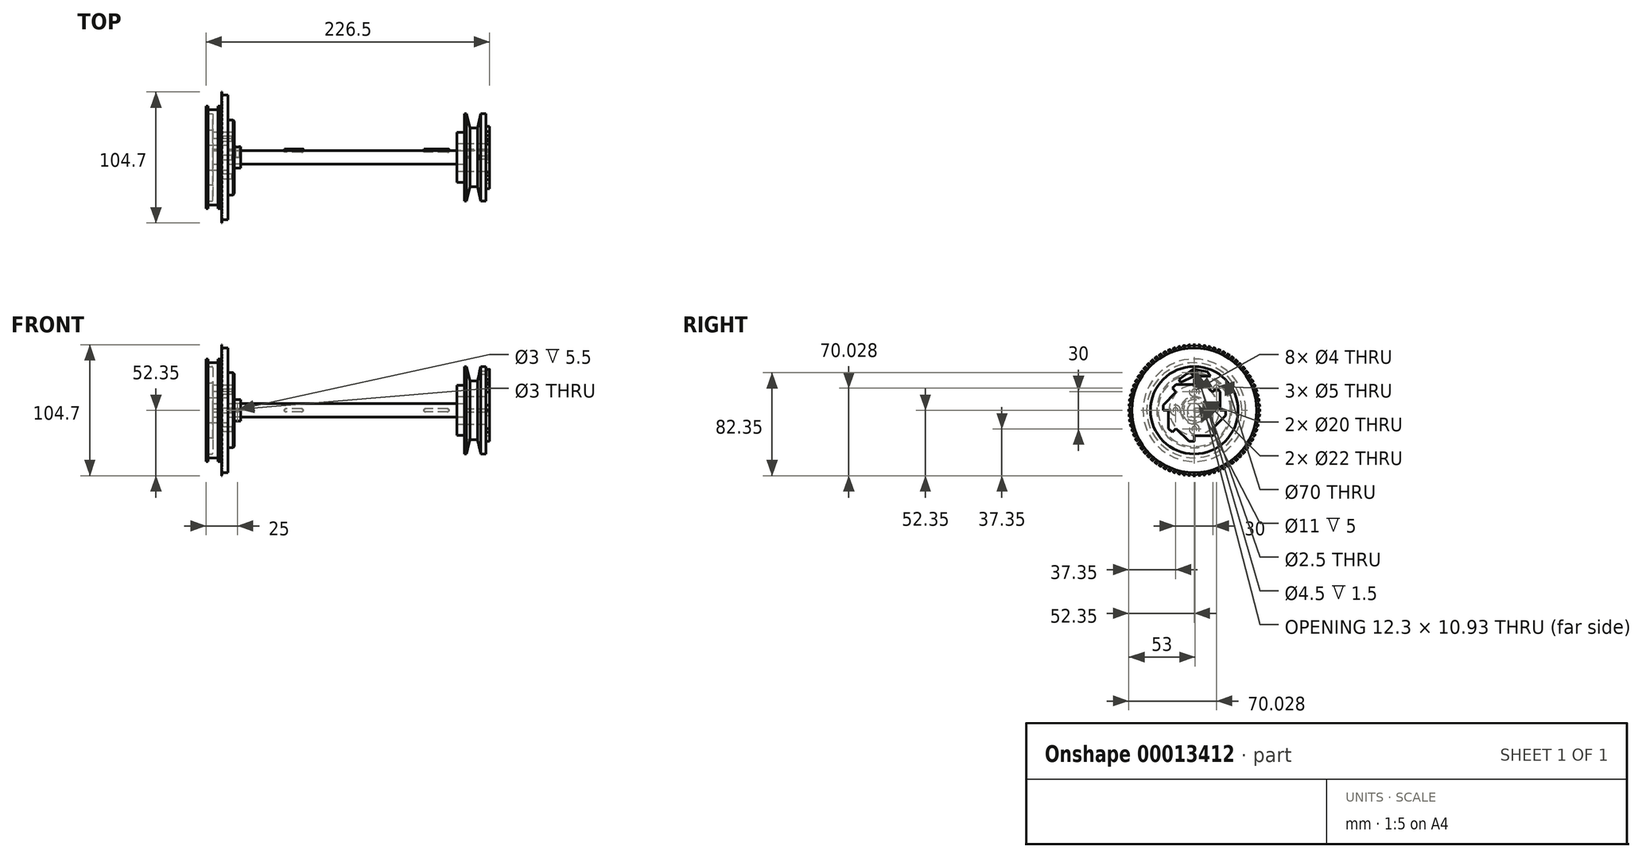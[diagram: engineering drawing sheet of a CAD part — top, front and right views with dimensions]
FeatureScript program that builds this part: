
annotation { "Feature Type Name" : "Feature", "Feature Type Description" : "" }
export const myFeature = defineFeature(function(context is Context, id is Id, definition is map)
    precondition{}
    {
        {
            var Q0;
            Q0=qCreatedBy(makeId("Right.planeOp"),FACE);
            var sketch = newSketch(context, id + "F0", { "sketchPlane" : qUnion([Q0])});
            skCircle(sketch, "E0", {"center": v(0, 0) * mm, "radius": 5.5 * mm});
            skSolve(sketch);
        }
        {
            var Q0;
            Q0=makeQuery(id+"F0.imprint","IMPRINT",FACE,{"disambiguationData":[TD([[makeQuery(id+"F0.imprint","IMPRINT",EDGE,{"derivedFrom":sQuery(id+"F0.wireOp",EDGE,"E0")}),1.0]])]});
            extrude(context, id + "F1", {"entities" : qUnion([Q0]), "endBound" : BoundingType.SYMMETRIC, "depth" : 204 * mm});
        }
        {
            var Q0;
            Q0=qCreatedBy(makeId("Front.planeOp"),FACE);
            cPlane(context, id + "F2", {"entities" : qUnion([Q0]), "cplaneType" : CPlaneType.OFFSET, "offset" : 5.5 * mm, "oppositeDirection" : true, "width" : 150 * mm, "height" : 150 * mm});
        }
        {
            var Q0;
            Q0=qCreatedBy(id+"F2.planeOp",FACE);
            var sketch = newSketch(context, id + "F3", { "sketchPlane" : qUnion([Q0])});
            skLineSegment(sketch, "E1.0", {"start": v(102, 5.5) * mm, "end": v(102, -5.5) * mm});
            skLineSegment(sketch, "E1.1", {"start": v(-102, 5.5) * mm, "end": v(-102, -5.5) * mm});
            skLineSegment(sketch, "E2", {"start": v(102, 0) * mm, "end": v(69.5, 0) * mm, "construction": true});
            skCircle(sketch, "E3", {"center": v(68.25, 0) * mm, "radius": 1.25 * mm});
            skCircle(sketch, "E4", {"center": v(50.75, 0) * mm, "radius": 1.25 * mm});
            skLineSegment(sketch, "E5", {"start": v(68.25, 1.25) * mm, "end": v(50.75, 1.25) * mm});
            skLineSegment(sketch, "E6", {"start": v(68.25, -1.25) * mm, "end": v(50.75, -1.25) * mm});
            skLineSegment(sketch, "E7", {"start": v(-102, 0) * mm, "end": v(-62, 0) * mm, "construction": true});
            skCircle(sketch, "E8", {"center": v(-60.75, 0) * mm, "radius": 1.25 * mm});
            skCircle(sketch, "E9", {"center": v(-48.25, 0) * mm, "radius": 1.25 * mm});
            skLineSegment(sketch, "E10", {"start": v(-48.25, 1.25) * mm, "end": v(-60.75, 1.25) * mm});
            skLineSegment(sketch, "E11", {"start": v(-48.25, -1.25) * mm, "end": v(-60.75, -1.25) * mm});
            skSolve(sketch);
        }
        {
            var Q0;
            {var subQ1=sQuery(id+"F3.wireOp",EDGE,"E5");Q0=makeQuery(id+"F3.imprint","IMPRINT",FACE,{"disambiguationData":[TD([[makeQuery(id+"F3.imprint","IMPRINT",EDGE,{"derivedFrom":subQ1}),1.0]])]});}
            var Q1;
            {var subQ0=sQuery(id+"F3.wireOp",EDGE,"E3");var subQ2=makeQuery(id+"F3.imprint","INTERSECT",VERTEX,{"derivedFrom":[subQ0,sQuery(id+"F3.wireOp",EDGE,"E5")]});Q1=makeQuery(id+"F3.imprint","IMPRINT",FACE,{"disambiguationData":[TD([[makeQuery(id+"F3.imprint","IMPRINT",EDGE,{"disambiguationData":[TD([[subQ2,-1.0]])],"derivedFrom":subQ0}),1.0]])]});}
            var Q2;
            {var subQ0=sQuery(id+"F3.wireOp",EDGE,"E4");var subQ2=makeQuery(id+"F3.imprint","INTERSECT",VERTEX,{"derivedFrom":[subQ0,sQuery(id+"F3.wireOp",EDGE,"E5")]});Q2=makeQuery(id+"F3.imprint","IMPRINT",FACE,{"disambiguationData":[TD([[makeQuery(id+"F3.imprint","IMPRINT",EDGE,{"disambiguationData":[TD([[subQ2,-1.0]])],"derivedFrom":subQ0}),1.0]])]});}
            var Q3;
            {var subQ0=sQuery(id+"F3.wireOp",EDGE,"E9");var subQ2=makeQuery(id+"F3.imprint","INTERSECT",VERTEX,{"derivedFrom":[subQ0,sQuery(id+"F3.wireOp",EDGE,"E10")]});Q3=makeQuery(id+"F3.imprint","IMPRINT",FACE,{"disambiguationData":[TD([[makeQuery(id+"F3.imprint","IMPRINT",EDGE,{"disambiguationData":[TD([[subQ2,-1.0]])],"derivedFrom":subQ0}),1.0]])]});}
            var Q4;
            {var subQ1=sQuery(id+"F3.wireOp",EDGE,"E10");Q4=makeQuery(id+"F3.imprint","IMPRINT",FACE,{"disambiguationData":[TD([[makeQuery(id+"F3.imprint","IMPRINT",EDGE,{"derivedFrom":subQ1}),1.0]])]});}
            var Q5;
            {var subQ0=sQuery(id+"F3.wireOp",EDGE,"E8");var subQ2=makeQuery(id+"F3.imprint","INTERSECT",VERTEX,{"derivedFrom":[subQ0,sQuery(id+"F3.wireOp",EDGE,"E10")]});Q5=makeQuery(id+"F3.imprint","IMPRINT",FACE,{"disambiguationData":[TD([[makeQuery(id+"F3.imprint","IMPRINT",EDGE,{"disambiguationData":[TD([[subQ2,-1.0]])],"derivedFrom":subQ0}),1.0]])]});}
            extrude(context, id + "F4", {"entities" : qUnion([Q0, Q1, Q2, Q3, Q4, Q5]), "operationType" : NewBodyOperationType.REMOVE, "depth" : 1.3 * mm});
        }
        {
            var Q0;
            {var subQ0=sQuery(id+"F3.wireOp",EDGE,"E3");var subQ2=makeQuery(id+"F3.imprint","INTERSECT",VERTEX,{"derivedFrom":[subQ0,sQuery(id+"F3.wireOp",EDGE,"E5")]});Q0=makeQuery(id+"F3.imprint","IMPRINT",FACE,{"disambiguationData":[TD([[makeQuery(id+"F3.imprint","IMPRINT",EDGE,{"disambiguationData":[TD([[subQ2,-1.0]])],"derivedFrom":subQ0}),1.0]])]});}
            var Q1;
            {var subQ1=sQuery(id+"F3.wireOp",EDGE,"E5");Q1=makeQuery(id+"F3.imprint","IMPRINT",FACE,{"disambiguationData":[TD([[makeQuery(id+"F3.imprint","IMPRINT",EDGE,{"derivedFrom":subQ1}),1.0]])]});}
            var Q2;
            {var subQ0=sQuery(id+"F3.wireOp",EDGE,"E4");var subQ2=makeQuery(id+"F3.imprint","INTERSECT",VERTEX,{"derivedFrom":[subQ0,sQuery(id+"F3.wireOp",EDGE,"E5")]});Q2=makeQuery(id+"F3.imprint","IMPRINT",FACE,{"disambiguationData":[TD([[makeQuery(id+"F3.imprint","IMPRINT",EDGE,{"disambiguationData":[TD([[subQ2,-1.0]])],"derivedFrom":subQ0}),1.0]])]});}
            var Q3;
            {var subQ0=sQuery(id+"F3.wireOp",EDGE,"E9");var subQ2=makeQuery(id+"F3.imprint","INTERSECT",VERTEX,{"derivedFrom":[subQ0,sQuery(id+"F3.wireOp",EDGE,"E10")]});Q3=makeQuery(id+"F3.imprint","IMPRINT",FACE,{"disambiguationData":[TD([[makeQuery(id+"F3.imprint","IMPRINT",EDGE,{"disambiguationData":[TD([[subQ2,-1.0]])],"derivedFrom":subQ0}),1.0]])]});}
            var Q4;
            {var subQ1=sQuery(id+"F3.wireOp",EDGE,"E10");Q4=makeQuery(id+"F3.imprint","IMPRINT",FACE,{"disambiguationData":[TD([[makeQuery(id+"F3.imprint","IMPRINT",EDGE,{"derivedFrom":subQ1}),1.0]])]});}
            var Q5;
            {var subQ0=sQuery(id+"F3.wireOp",EDGE,"E8");var subQ2=makeQuery(id+"F3.imprint","INTERSECT",VERTEX,{"derivedFrom":[subQ0,sQuery(id+"F3.wireOp",EDGE,"E10")]});Q5=makeQuery(id+"F3.imprint","IMPRINT",FACE,{"disambiguationData":[TD([[makeQuery(id+"F3.imprint","IMPRINT",EDGE,{"disambiguationData":[TD([[subQ2,-1.0]])],"derivedFrom":subQ0}),1.0]])]});}
            extrude(context, id + "F5", {"entities" : qUnion([Q0, Q1, Q2, Q3, Q4, Q5]), "endBound" : BoundingType.SYMMETRIC, "depth" : 2.5 * mm});
        }
        {
            var Q0;
            Q0=makeQuery(id+"F1.opExtrude","CAP_FACE",FACE,{"disambiguationData":[OSD([sQuery(id+"F0.wireOp",EDGE,"E0")])],"isStart":true});
            var sketch = newSketch(context, id + "F6", { "sketchPlane" : qUnion([Q0])});
            skCircle(sketch, "E12", {"center": v(0, 0) * mm, "radius": 10 * mm});
            skCircle(sketch, "E13", {"center": v(0, 0) * mm, "radius": 30 * mm});
            skLineSegment(sketch, "E14", {"start": v(0, 0) * mm, "end": v(0, -15) * mm, "construction": true});
            skLineSegment(sketch, "E15", {"start": v(0, 0) * mm, "end": v(-17.68, 17.68) * mm, "construction": true});
            skLineSegment(sketch, "E16", {"start": v(0, 0) * mm, "end": v(-5.5, 0) * mm, "construction": true});
            skCircle(sketch, "E17", {"center": v(0, -15) * mm, "radius": 2 * mm});
            skCircle(sketch, "E18", {"center": v(-17.68, 17.68) * mm, "radius": 2.5 * mm});
            skLineSegment(sketch, "E19.rect.bottom", {"start": v(-6.8, -1.25) * mm, "end": v(-4.2, -1.25) * mm});
            skLineSegment(sketch, "E19.rect.top", {"start": v(-6.8, 1.25) * mm, "end": v(-4.2, 1.25) * mm});
            skLineSegment(sketch, "E19.rect.left", {"start": v(-6.8, -1.25) * mm, "end": v(-6.8, 1.25) * mm});
            skLineSegment(sketch, "E19.rect.right", {"start": v(-4.2, -1.25) * mm, "end": v(-4.2, 1.25) * mm});
            skPoint(sketch, "E19.rect.middle", {"position": v(-5.5, 0) * mm});
            skCircle(sketch, "E20.1.0", {"center": v(15, 0) * mm, "radius": 2 * mm});
            skCircle(sketch, "E20.2.0", {"center": v(0, 15) * mm, "radius": 2 * mm});
            skCircle(sketch, "E20.3.0", {"center": v(-15, 0) * mm, "radius": 2 * mm});
            skSolve(sketch);
        }
        {
            var Q0;
            Q0=makeQuery(id+"F6.imprint","IMPRINT",FACE,{"disambiguationData":[TD([[makeQuery(id+"F6.imprint","IMPRINT",EDGE,{"derivedFrom":sQuery(id+"F6.wireOp",EDGE,"E12")}),-1.0]])]});
            extrude(context, id + "F7", {"entities" : qUnion([Q0]), "depth" : 5 * mm});
        }
        {
            var Q0;
            Q0=makeQuery(id+"F6.imprint","IMPRINT",FACE,{"disambiguationData":[TD([[makeQuery(id+"F6.imprint","IMPRINT",EDGE,{"derivedFrom":sQuery(id+"F6.wireOp",EDGE,"E12")}),1.0]])]});
            extrude(context, id + "F8", {"entities" : qUnion([Q0]), "operationType" : NewBodyOperationType.ADD, "depth" : 17 * mm});
        }
        {
            var Q0;
            Q0=makeQuery(id+"F7.opExtrude","CAP_EDGE",EDGE,{"disambiguationData":[OSD([sQuery(id+"F6.wireOp",EDGE,"E13")])],"isStart":true});
            chamfer(context, id + "F9", {"entities" : qUnion([Q0]), "width" : 1 * mm, "tangentPropagation" : true});
        }
        {
            var Q0;
            Q0=makeQuery(id+"F7.opExtrude","CAP_EDGE",EDGE,{"disambiguationData":[OSD([sQuery(id+"F6.wireOp",EDGE,"E20.1.0")])],"isStart":true});
            var Q1;
            Q1=makeQuery(id+"F7.opExtrude","CAP_EDGE",EDGE,{"disambiguationData":[OSD([sQuery(id+"F6.wireOp",EDGE,"E17")])],"isStart":true});
            var Q2;
            Q2=makeQuery(id+"F7.opExtrude","CAP_EDGE",EDGE,{"disambiguationData":[OSD([sQuery(id+"F6.wireOp",EDGE,"E20.3.0")])],"isStart":true});
            var Q3;
            Q3=makeQuery(id+"F7.opExtrude","CAP_EDGE",EDGE,{"disambiguationData":[OSD([sQuery(id+"F6.wireOp",EDGE,"E20.2.0")])],"isStart":true});
            chamfer(context, id + "F10", {"entities" : qUnion([Q0, Q1, Q2, Q3]), "width" : 2 * mm, "tangentPropagation" : true});
        }
        {
            var Q0;
            Q0=makeQuery(id+"F1.opExtrude","CAP_FACE",FACE,{"disambiguationData":[OSD([sQuery(id+"F0.wireOp",EDGE,"E0")])],"isStart":false});
            var sketch = newSketch(context, id + "F11", { "sketchPlane" : qUnion([Q0])});
            skLineSegment(sketch, "E21.0", {"start": v(4.25, 1.25) * mm, "end": v(6.75, 1.25) * mm});
            skLineSegment(sketch, "E21.1", {"start": v(4.25, -1.25) * mm, "end": v(6.75, -1.25) * mm});
            skCircle(sketch, "E22", {"center": v(0, 0) * mm, "radius": 11 * mm});
            skCircle(sketch, "E23", {"center": v(0, 0) * mm, "radius": 20.5 * mm});
            skCircle(sketch, "E24", {"center": v(0, 0) * mm, "radius": 25.25 * mm});
            skLineSegment(sketch, "E25", {"start": v(0, 0) * mm, "end": v(5.5, 0) * mm, "construction": true});
            skLineSegment(sketch, "E26.rect.bottom", {"start": v(6.8, -1.25) * mm, "end": v(4.2, -1.25) * mm});
            skLineSegment(sketch, "E26.rect.top", {"start": v(6.8, 1.25) * mm, "end": v(4.2, 1.25) * mm});
            skLineSegment(sketch, "E26.rect.left", {"start": v(6.8, -1.25) * mm, "end": v(6.8, 1.25) * mm});
            skLineSegment(sketch, "E26.rect.right", {"start": v(4.2, -1.25) * mm, "end": v(4.2, 1.25) * mm});
            skPoint(sketch, "E26.rect.middle", {"position": v(5.5, 0) * mm});
            skLineSegment(sketch, "E27", {"start": v(20.5, 0) * mm, "end": v(25.25, 0) * mm});
            skLineSegment(sketch, "E28.1.0", {"start": v(14.5, 14.5) * mm, "end": v(17.85, 17.85) * mm});
            skLineSegment(sketch, "E28.2.0", {"start": v(0, 20.5) * mm, "end": v(0, 25.25) * mm});
            skLineSegment(sketch, "E28.3.0", {"start": v(-14.5, 14.5) * mm, "end": v(-17.85, 17.85) * mm});
            skLineSegment(sketch, "E28.4.0", {"start": v(-20.5, 0) * mm, "end": v(-25.25, 0) * mm});
            skLineSegment(sketch, "E28.5.0", {"start": v(-14.5, -14.5) * mm, "end": v(-17.85, -17.85) * mm});
            skLineSegment(sketch, "E28.6.0", {"start": v(0, -20.5) * mm, "end": v(0, -25.25) * mm});
            skLineSegment(sketch, "E28.7.0", {"start": v(14.5, -14.5) * mm, "end": v(17.85, -17.85) * mm});
            skLineSegment(sketch, "E29", {"start": v(0, -20.5) * mm, "end": v(14.74, -20.5) * mm});
            skLineSegment(sketch, "E30", {"start": v(14.74, -20.5) * mm, "end": v(17.62, -17.62) * mm});
            skLineSegment(sketch, "E31.1.0", {"start": v(14.5, -14.5) * mm, "end": v(24.92, -4.07) * mm});
            skLineSegment(sketch, "E31.1.1", {"start": v(24.92, -4.07) * mm, "end": v(24.92, 0) * mm});
            skLineSegment(sketch, "E31.2.0", {"start": v(20.5, 0) * mm, "end": v(20.5, 14.74) * mm});
            skLineSegment(sketch, "E31.2.1", {"start": v(20.5, 14.74) * mm, "end": v(17.62, 17.62) * mm});
            skLineSegment(sketch, "E31.3.0", {"start": v(14.5, 14.5) * mm, "end": v(4.07, 24.92) * mm});
            skLineSegment(sketch, "E31.3.1", {"start": v(4.07, 24.92) * mm, "end": v(0, 24.92) * mm});
            skLineSegment(sketch, "E31.4.0", {"start": v(0, 20.5) * mm, "end": v(-14.74, 20.5) * mm});
            skLineSegment(sketch, "E31.4.1", {"start": v(-14.74, 20.5) * mm, "end": v(-17.62, 17.62) * mm});
            skLineSegment(sketch, "E31.5.0", {"start": v(-14.5, 14.5) * mm, "end": v(-24.92, 4.07) * mm});
            skLineSegment(sketch, "E31.5.1", {"start": v(-24.92, 4.07) * mm, "end": v(-24.92, 0) * mm});
            skLineSegment(sketch, "E31.6.0", {"start": v(-20.5, 0) * mm, "end": v(-20.5, -14.74) * mm});
            skLineSegment(sketch, "E31.6.1", {"start": v(-20.5, -14.74) * mm, "end": v(-17.62, -17.62) * mm});
            skLineSegment(sketch, "E31.7.0", {"start": v(-14.5, -14.5) * mm, "end": v(-4.07, -24.92) * mm});
            skLineSegment(sketch, "E31.7.1", {"start": v(-4.07, -24.92) * mm, "end": v(0, -24.92) * mm});
            skSolve(sketch);
        }
        {
            var Q0;
            {var subQ1=sQuery(id+"F11.wireOp",EDGE,"E31.5.0");Q0=makeQuery(id+"F11.imprint","IMPRINT",FACE,{"disambiguationData":[TD([[makeQuery(id+"F11.imprint","IMPRINT",EDGE,{"derivedFrom":subQ1}),1.0]])]});}
            var Q1;
            {var subQ1=sQuery(id+"F11.wireOp",EDGE,"E31.4.0");Q1=makeQuery(id+"F11.imprint","IMPRINT",FACE,{"disambiguationData":[TD([[makeQuery(id+"F11.imprint","IMPRINT",EDGE,{"derivedFrom":subQ1}),1.0]])]});}
            var Q2;
            {var subQ1=sQuery(id+"F11.wireOp",EDGE,"E31.3.0");Q2=makeQuery(id+"F11.imprint","IMPRINT",FACE,{"disambiguationData":[TD([[makeQuery(id+"F11.imprint","IMPRINT",EDGE,{"derivedFrom":subQ1}),1.0]])]});}
            var Q3;
            {var subQ1=sQuery(id+"F11.wireOp",EDGE,"E31.2.0");Q3=makeQuery(id+"F11.imprint","IMPRINT",FACE,{"disambiguationData":[TD([[makeQuery(id+"F11.imprint","IMPRINT",EDGE,{"derivedFrom":subQ1}),1.0]])]});}
            var Q4;
            {var subQ1=sQuery(id+"F11.wireOp",EDGE,"E31.1.0");Q4=makeQuery(id+"F11.imprint","IMPRINT",FACE,{"disambiguationData":[TD([[makeQuery(id+"F11.imprint","IMPRINT",EDGE,{"derivedFrom":subQ1}),1.0]])]});}
            var Q5;
            {var subQ1=sQuery(id+"F11.wireOp",EDGE,"E29");Q5=makeQuery(id+"F11.imprint","IMPRINT",FACE,{"disambiguationData":[TD([[makeQuery(id+"F11.imprint","IMPRINT",EDGE,{"derivedFrom":subQ1}),1.0]])]});}
            var Q6;
            {var subQ1=sQuery(id+"F11.wireOp",EDGE,"E31.7.0");Q6=makeQuery(id+"F11.imprint","IMPRINT",FACE,{"disambiguationData":[TD([[makeQuery(id+"F11.imprint","IMPRINT",EDGE,{"derivedFrom":subQ1}),1.0]])]});}
            var Q7;
            {var subQ1=sQuery(id+"F11.wireOp",EDGE,"E31.6.0");Q7=makeQuery(id+"F11.imprint","IMPRINT",FACE,{"disambiguationData":[TD([[makeQuery(id+"F11.imprint","IMPRINT",EDGE,{"derivedFrom":subQ1}),1.0]])]});}
            var Q8;
            Q8=makeQuery(id+"F11.imprint","IMPRINT",FACE,{"disambiguationData":[TD([[makeQuery(id+"F11.imprint","IMPRINT",EDGE,{"derivedFrom":sQuery(id+"F11.wireOp",EDGE,"E22")}),-1.0]])]});
            extrude(context, id + "F12", {"entities" : qUnion([Q0, Q1, Q2, Q3, Q4, Q5, Q6, Q7, Q8]), "oppositeDirection" : true, "depth" : 3 * mm});
        }
        {
            var Q0;
            Q0=makeQuery(id+"F11.imprint","IMPRINT",FACE,{"disambiguationData":[TD([[makeQuery(id+"F11.imprint","IMPRINT",EDGE,{"derivedFrom":sQuery(id+"F11.wireOp",EDGE,"E22")}),1.0]])]});
            extrude(context, id + "F13", {"entities" : qUnion([Q0]), "operationType" : NewBodyOperationType.ADD, "oppositeDirection" : true, "depth" : 20 * mm});
        }
        {
            var Q0;
            Q0=makeQuery(id+"F7.opExtrude","CAP_FACE",FACE,{"disambiguationData":[OSD([sQuery(id+"F6.wireOp",EDGE,"E12"),sQuery(id+"F6.wireOp",EDGE,"E13"),sQuery(id+"F6.wireOp",EDGE,"E17"),sQuery(id+"F6.wireOp",EDGE,"E18"),sQuery(id+"F6.wireOp",EDGE,"E20.1.0"),sQuery(id+"F6.wireOp",EDGE,"E20.2.0"),sQuery(id+"F6.wireOp",EDGE,"E20.3.0")])],"isStart":false});
            var sketch = newSketch(context, id + "F14", { "sketchPlane" : qUnion([Q0])});
            skCircle(sketch, "E32", {"center": v(0, 0) * mm, "radius": 52.35 * mm});
            skCircle(sketch, "E33", {"center": v(0, 0) * mm, "radius": 51.1 * mm, "construction": true});
            skCircle(sketch, "E34", {"center": v(0, 0) * mm, "radius": 49.85 * mm});
            skLineSegment(sketch, "E35", {"start": v(0, 0) * mm, "end": v(0, 52.35) * mm, "construction": true});
            skLineSegment(sketch, "E36", {"start": v(0, 49.85) * mm, "end": v(15, 49.85) * mm, "construction": true});
            skLineSegment(sketch, "E37", {"start": v(0, 0) * mm, "end": v(-1, 51.1) * mm, "construction": true});
            skLineSegment(sketch, "E38", {"start": v(0, 0) * mm, "end": v(-3.15, 49.75) * mm, "construction": true});
            skArc(sketch, "E39", {"start": v(-0.86, 52.34) * mm, "mid": v(-1, 51.1) * mm, "end": v(-1.05, 49.84) * mm});
            skArc(sketch, "E40.0.MirrorCS", {"start": v(0.86, 52.34) * mm, "mid": v(1, 51.1) * mm, "end": v(1.05, 49.84) * mm});
            skSolve(sketch);
        }
        {
            var Q0;
            Q0=makeQuery(id+"F14.imprint","IMPRINT",FACE,{"disambiguationData":[TD([[makeQuery(id+"F14.imprint","IMPRINT",EDGE,{"derivedFrom":makeQuery(id+"F7.opExtrude","CAP_EDGE",EDGE,{"disambiguationData":[OSD([sQuery(id+"F6.wireOp",EDGE,"E13")])],"isStart":false})}),-1.0]])]});
            var Q1;
            {var subQ1=sQuery(id+"F14.wireOp",EDGE,"E39");Q1=makeQuery(id+"F14.imprint","IMPRINT",FACE,{"disambiguationData":[TD([[makeQuery(id+"F14.imprint","IMPRINT",EDGE,{"derivedFrom":subQ1}),1.0]])]});}
            var Q2;
            Q2=makeQuery(id+"F14.imprint","IMPRINT",FACE,{"disambiguationData":[TD([[makeQuery(id+"F14.imprint","IMPRINT",EDGE,{"derivedFrom":makeQuery(id+"F7.opExtrude","CAP_EDGE",EDGE,{"disambiguationData":[OSD([sQuery(id+"F6.wireOp",EDGE,"E13")])],"isStart":false})}),1.0]])]});
            extrude(context, id + "F15", {"entities" : qUnion([Q0, Q1, Q2]), "depth" : 5 * mm});
        }
        {
            var Q0;
            Q0=makeQuery(id+"F15.opExtrude","SWEPT_FACE",FACE,{"disambiguationData":[OSD([sQuery(id+"F14.wireOp",EDGE,"E40.0.MirrorCS")])]});
            var Q1;
            Q1=makeQuery(id+"F15.opExtrude","SWEPT_FACE",FACE,{"disambiguationData":[OSD([sQuery(id+"F14.wireOp",EDGE,"E32")])]});
            var Q2;
            Q2=makeQuery(id+"F15.opExtrude","SWEPT_FACE",FACE,{"disambiguationData":[OSD([sQuery(id+"F14.wireOp",EDGE,"E39")])]});
            var Q3;
            Q3=makeQuery(id+"F8.opExtrude","CAP_EDGE",EDGE,{"disambiguationData":[OSD([sQuery(id+"F6.wireOp",EDGE,"E12")])],"isStart":false});
            circularPattern(context, id + "F16", {"faces" : qUnion([Q0, Q1, Q2]), "axis" : qUnion([Q3]), "angle" : 4.5 * degree, "instanceCount" : round(80), "patternType" : PatternType.FACE});
        }
        {
            var Q0;
            Q0=qCreatedBy(makeId("Front.planeOp"),FACE);
            var sketch = newSketch(context, id + "F17", { "sketchPlane" : qUnion([Q0])});
            skLineSegment(sketch, "E41.0", {"start": v(-107, -30) * mm, "end": v(-107, 30) * mm});
            skLineSegment(sketch, "E42", {"start": v(-107, 0) * mm, "end": v(-134.37, 0) * mm, "construction": true});
            skLineSegment(sketch, "E43", {"start": v(-107, 0) * mm, "end": v(-107, 49.85) * mm, "construction": true});
            skLineSegment(sketch, "E44.bottom", {"start": v(-107, 49.85) * mm, "end": v(-112, 49.85) * mm});
            skLineSegment(sketch, "E44.top", {"start": v(-107, 52.35) * mm, "end": v(-112, 52.35) * mm});
            skLineSegment(sketch, "E44.left", {"start": v(-107, 49.85) * mm, "end": v(-107, 52.35) * mm});
            skLineSegment(sketch, "E44.right", {"start": v(-112, 49.85) * mm, "end": v(-112, 52.35) * mm});
            skLineSegment(sketch, "E45", {"start": v(-109.5, 52.35) * mm, "end": v(-109.5, 49.85) * mm, "construction": true});
            skLineSegment(sketch, "E46", {"start": v(-107, 49.85) * mm, "end": v(-117, 49.85) * mm, "construction": true});
            skLineSegment(sketch, "E47", {"start": v(-107, 51.1) * mm, "end": v(-112, 51.1) * mm, "construction": true});
            skArc(sketch, "E48", {"start": v(-107, 51.1) * mm, "mid": v(-107.1, 51.73) * mm, "end": v(-107.24, 52.35) * mm});
            skArc(sketch, "E49.0.MirrorCS", {"start": v(-112, 51.1) * mm, "mid": v(-111.9, 51.73) * mm, "end": v(-111.76, 52.35) * mm});
            skSolve(sketch);
        }
        {
            var Q0;
            {var subQ0=sQuery(id+"F17.wireOp",EDGE,"E49.0.MirrorCS");Q0=makeQuery(id+"F17.imprint","IMPRINT",FACE,{"disambiguationData":[TD([[makeQuery(id+"F17.imprint","IMPRINT",EDGE,{"derivedFrom":subQ0}),1.0]])]});}
            var Q1;
            {var subQ0=sQuery(id+"F17.wireOp",EDGE,"E48");Q1=makeQuery(id+"F17.imprint","IMPRINT",FACE,{"disambiguationData":[TD([[makeQuery(id+"F17.imprint","IMPRINT",EDGE,{"derivedFrom":subQ0}),-1.0]])]});}
            var Q2;
            Q2=sQuery(id+"F17.wireOp",EDGE,"E42");
            revolve(context, id + "F18", {"operationType" : NewBodyOperationType.REMOVE, "entities" : qUnion([Q0, Q1]), "axis" : qUnion([Q2]), "revolveType" : RevolveType.FULL, "oppositeDirection" : true});
        }
        {
            var Q0;
            Q0=qCreatedBy(makeId("Front.planeOp"),FACE);
            var sketch = newSketch(context, id + "F19", { "sketchPlane" : qUnion([Q0])});
            skLineSegment(sketch, "E50.0", {"start": v(-112, -10) * mm, "end": v(-112, 10) * mm});
            skLineSegment(sketch, "E51", {"start": v(-112, 0) * mm, "end": v(-131.3, 0) * mm, "construction": true});
            skLineSegment(sketch, "E52", {"start": v(-112, 10) * mm, "end": v(-112, 22) * mm});
            skLineSegment(sketch, "E53", {"start": v(-112, 22) * mm, "end": v(-113.5, 22) * mm});
            skLineSegment(sketch, "E54", {"start": v(-113.5, 22) * mm, "end": v(-113.5, 41) * mm});
            skLineSegment(sketch, "E55", {"start": v(-113.5, 41) * mm, "end": v(-115, 41) * mm});
            skLineSegment(sketch, "E56", {"start": v(-115, 41) * mm, "end": v(-115, 38) * mm});
            skLineSegment(sketch, "E57", {"start": v(-115, 38) * mm, "end": v(-123, 38) * mm});
            skLineSegment(sketch, "E58", {"start": v(-123, 38) * mm, "end": v(-123, 41) * mm});
            skLineSegment(sketch, "E59", {"start": v(-123, 41) * mm, "end": v(-124.5, 41) * mm});
            skLineSegment(sketch, "E60", {"start": v(-124.5, 41) * mm, "end": v(-124.5, 35) * mm});
            skLineSegment(sketch, "E61", {"start": v(-124.5, 35) * mm, "end": v(-119, 35) * mm});
            skLineSegment(sketch, "E62", {"start": v(-119, 35) * mm, "end": v(-119, 22) * mm});
            skLineSegment(sketch, "E63", {"start": v(-119, 22) * mm, "end": v(-124.5, 22) * mm});
            skLineSegment(sketch, "E64", {"start": v(-124.5, 22) * mm, "end": v(-124.5, 10) * mm});
            skLineSegment(sketch, "E65", {"start": v(-124.5, 10) * mm, "end": v(-112, 10) * mm});
            skSolve(sketch);
        }
        {
            var Q0;
            Q0=makeQuery(id+"F19.imprint","IMPRINT",FACE,{"disambiguationData":[TD([[makeQuery(id+"F19.imprint","IMPRINT",EDGE,{"derivedFrom":sQuery(id+"F19.wireOp",EDGE,"E52")}),1.0]])]});
            var Q1;
            Q1=sQuery(id+"F19.wireOp",EDGE,"E51");
            revolve(context, id + "F20", {"entities" : qUnion([Q0]), "axis" : qUnion([Q1]), "revolveType" : RevolveType.FULL});
        }
        {
            var Q0;
            Q0=makeQuery(id+"F20.opRevolve","SWEPT_EDGE",EDGE,{"disambiguationData":[OSD([sQuery(id+"F19.wireOp",EDGE,"E53"),sQuery(id+"F19.wireOp",EDGE,"E54")])]});
            var Q1;
            Q1=makeQuery(id+"F20.opRevolve","SWEPT_EDGE",EDGE,{"disambiguationData":[OSD([sQuery(id+"F19.wireOp",EDGE,"E62"),sQuery(id+"F19.wireOp",EDGE,"E63")])]});
            var Q2;
            Q2=makeQuery(id+"F20.opRevolve","SWEPT_EDGE",EDGE,{"disambiguationData":[OSD([sQuery(id+"F19.wireOp",EDGE,"E61"),sQuery(id+"F19.wireOp",EDGE,"E62")])]});
            var Q3;
            Q3=makeQuery(id+"F20.opRevolve","SWEPT_EDGE",EDGE,{"disambiguationData":[OSD([sQuery(id+"F19.wireOp",EDGE,"E63"),sQuery(id+"F19.wireOp",EDGE,"E64")])]});
            var Q4;
            Q4=makeQuery(id+"F20.opRevolve","SWEPT_EDGE",EDGE,{"disambiguationData":[OSD([sQuery(id+"F19.wireOp",EDGE,"E60"),sQuery(id+"F19.wireOp",EDGE,"E61")])]});
            fillet(context, id + "F21", {"entities" : qUnion([Q0, Q1, Q2, Q3, Q4]), "radius" : 1 * mm, "tangentPropagation" : true, "allowEdgeOverflow" : false});
        }
        {
            var Q0;
            Q0=makeQuery(id+"F20.opRevolve","SWEPT_FACE",FACE,{"disambiguationData":[OSD([sQuery(id+"F19.wireOp",EDGE,"E54")])]});
            var sketch = newSketch(context, id + "F22", { "sketchPlane" : qUnion([Q0])});
            skCircle(sketch, "E66.0", {"center": v(17.68, 17.68) * mm, "radius": 2.5 * mm});
            skSolve(sketch);
        }
        {
            var Q0;
            {var subQ0=sQuery(id+"F19.wireOp",EDGE,"E54");var subQ1=makeQuery(id+"F21.opFillet","BLEND_EDGE",EDGE,{"blendedFrom":[makeQuery(id+"F20.opRevolve","SWEPT_EDGE",EDGE,{"disambiguationData":[OSD([sQuery(id+"F19.wireOp",EDGE,"E53"),subQ0])]}),makeQuery(id+"F20.opRevolve","SWEPT_FACE",FACE,{"disambiguationData":[OSD([subQ0])]})],"blendedInto":[makeQuery(id+"F20.opRevolve","SWEPT_FACE",FACE,{"disambiguationData":[OSD([subQ0])]})]});var subQ2=sQuery(id+"F22.wireOp",EDGE,"E66.0");var subQ4=makeQuery(id+"F22.imprint","INTERSECT",VERTEX,{"disambiguationData":[OD(0.0)],"derivedFrom":[subQ1,subQ2]});Q0=makeQuery(id+"F22.imprint","IMPRINT",FACE,{"disambiguationData":[TD([[makeQuery(id+"F22.imprint","IMPRINT",EDGE,{"disambiguationData":[TD([[subQ4,1.0]])],"derivedFrom":subQ2}),1.0]])]});}
            var Q1;
            {var subQ0=sQuery(id+"F19.wireOp",EDGE,"E54");var subQ1=makeQuery(id+"F21.opFillet","BLEND_EDGE",EDGE,{"blendedFrom":[makeQuery(id+"F20.opRevolve","SWEPT_EDGE",EDGE,{"disambiguationData":[OSD([sQuery(id+"F19.wireOp",EDGE,"E53"),subQ0])]}),makeQuery(id+"F20.opRevolve","SWEPT_FACE",FACE,{"disambiguationData":[OSD([subQ0])]})],"blendedInto":[makeQuery(id+"F20.opRevolve","SWEPT_FACE",FACE,{"disambiguationData":[OSD([subQ0])]})]});var subQ2=sQuery(id+"F22.wireOp",EDGE,"E66.0");var subQ4=makeQuery(id+"F22.imprint","INTERSECT",VERTEX,{"disambiguationData":[OD(0.0)],"derivedFrom":[subQ1,subQ2]});Q1=makeQuery(id+"F22.imprint","IMPRINT",FACE,{"disambiguationData":[TD([[makeQuery(id+"F22.imprint","IMPRINT",EDGE,{"disambiguationData":[TD([[subQ4,-1.0]])],"derivedFrom":subQ2}),1.0]])]});}
            extrude(context, id + "F23", {"entities" : qUnion([Q0, Q1]), "operationType" : NewBodyOperationType.REMOVE, "endBound" : BoundingType.SYMMETRIC, "oppositeDirection" : true, "depth" : 13 * mm});
        }
        {
            var Q0;
            Q0=qCreatedBy(makeId("Front.planeOp"),FACE);
            var sketch = newSketch(context, id + "F24", { "sketchPlane" : qUnion([Q0])});
            skLineSegment(sketch, "E67.0", {"start": v(82, 11) * mm, "end": v(82, -11) * mm});
            skLineSegment(sketch, "E67.1", {"start": v(99, 11) * mm, "end": v(99, -11) * mm});
            skLineSegment(sketch, "E68", {"start": v(99, 0) * mm, "end": v(82, 0) * mm, "construction": true});
            skLineSegment(sketch, "E69", {"start": v(99, 11) * mm, "end": v(99, 35) * mm});
            skLineSegment(sketch, "E70", {"start": v(99, 35) * mm, "end": v(95, 35) * mm});
            skLineSegment(sketch, "E71", {"start": v(95, 35) * mm, "end": v(92.25, 23.5) * mm});
            skLineSegment(sketch, "E72", {"start": v(92.25, 23.5) * mm, "end": v(86.25, 23.5) * mm});
            skLineSegment(sketch, "E73", {"start": v(86.25, 23.5) * mm, "end": v(83.5, 35) * mm});
            skLineSegment(sketch, "E74", {"start": v(83.5, 35) * mm, "end": v(82, 35) * mm});
            skLineSegment(sketch, "E75", {"start": v(82, 35) * mm, "end": v(82, 11) * mm});
            skLineSegment(sketch, "E76", {"start": v(82, 11) * mm, "end": v(99, 11) * mm});
            skSolve(sketch);
        }
        {
            var Q0;
            Q0=makeQuery(id+"F24.imprint","IMPRINT",FACE,{"disambiguationData":[TD([[makeQuery(id+"F24.imprint","IMPRINT",EDGE,{"derivedFrom":sQuery(id+"F24.wireOp",EDGE,"E69")}),1.0]])]});
            var Q1;
            Q1=sQuery(id+"F24.wireOp",EDGE,"E68");
            revolve(context, id + "F25", {"entities" : qUnion([Q0]), "axis" : qUnion([Q1]), "revolveType" : RevolveType.FULL});
        }
        {
            var Q0;
            Q0=makeQuery(id+"F25.opRevolve","SWEPT_FACE",FACE,{"disambiguationData":[OSD([sQuery(id+"F24.wireOp",EDGE,"E69")])]});
            var sketch = newSketch(context, id + "F26", { "sketchPlane" : qUnion([Q0])});
            skLineSegment(sketch, "E77", {"start": v(0, 0) * mm, "end": v(0, 30) * mm, "construction": true});
            skCircle(sketch, "E78", {"center": v(0, 30) * mm, "radius": 1.25 * mm});
            skSolve(sketch);
        }
        {
            var Q0;
            Q0=makeQuery(id+"F26.imprint","IMPRINT",FACE,{"disambiguationData":[TD([[makeQuery(id+"F26.imprint","IMPRINT",EDGE,{"derivedFrom":sQuery(id+"F26.wireOp",EDGE,"E78")}),1.0]])]});
            extrude(context, id + "F27", {"entities" : qUnion([Q0]), "operationType" : NewBodyOperationType.REMOVE, "oppositeDirection" : true, "depth" : 8 * mm});
        }
        {
            var Q0;
            Q0=makeQuery(id+"F25.opRevolve","SWEPT_FACE",FACE,{"disambiguationData":[OSD([sQuery(id+"F24.wireOp",EDGE,"E75")])]});
            var sketch = newSketch(context, id + "F28", { "sketchPlane" : qUnion([Q0])});
            skCircle(sketch, "E79.0", {"center": v(0, 0) * mm, "radius": 23.5 * mm});
            skLineSegment(sketch, "E80", {"start": v(0, 0) * mm, "end": v(0, -23.5) * mm, "construction": true});
            skCircle(sketch, "E81", {"center": v(0, -24.25) * mm, "radius": 0.75 * mm});
            skSolve(sketch);
        }
        {
            var Q0;
            Q0=makeQuery(id+"F28.imprint","IMPRINT",FACE,{"disambiguationData":[TD([[makeQuery(id+"F28.imprint","IMPRINT",EDGE,{"derivedFrom":sQuery(id+"F28.wireOp",EDGE,"E81")}),1.0]])]});
            extrude(context, id + "F29", {"entities" : qUnion([Q0]), "operationType" : NewBodyOperationType.REMOVE, "oppositeDirection" : true, "depth" : 8 * mm});
        }
        {
            var Q0;
            Q0=makeQuery(id+"F13.opExtrude","CAP_FACE",FACE,{"disambiguationData":[OSD([sQuery(id+"F0.wireOp",EDGE,"E0"),sQuery(id+"F11.wireOp",EDGE,"E22"),sQuery(id+"F11.wireOp",EDGE,"E26.rect.bottom"),sQuery(id+"F11.wireOp",EDGE,"E26.rect.top"),sQuery(id+"F11.wireOp",EDGE,"E26.rect.left")])],"isStart":false});
            var sketch = newSketch(context, id + "F30", { "sketchPlane" : qUnion([Q0])});
            skCircle(sketch, "E82.0", {"center": v(0, 0) * mm, "radius": 5.5 * mm});
            skCircle(sketch, "E83", {"center": v(0, 0) * mm, "radius": 20 * mm});
            skSolve(sketch);
        }
        {
            var Q0;
            Q0=makeQuery(id+"F30.imprint","IMPRINT",FACE,{"disambiguationData":[TD([[makeQuery(id+"F30.imprint","IMPRINT",EDGE,{"derivedFrom":sQuery(id+"F30.wireOp",EDGE,"E83")}),1.0]])]});
            var Q1;
            Q1=makeQuery(id+"F30.imprint","IMPRINT",FACE,{"disambiguationData":[TD([[makeQuery(id+"F30.imprint","IMPRINT",EDGE,{"disambiguationData":[OD(0.0)],"derivedFrom":sQuery(id+"F30.wireOp",EDGE,"E82.0")}),1.0]])]});
            var Q2;
            Q2=makeQuery(id+"F30.imprint","IMPRINT",FACE,{"disambiguationData":[TD([[makeQuery(id+"F30.imprint","IMPRINT",EDGE,{"disambiguationData":[OD(1.0)],"derivedFrom":sQuery(id+"F30.wireOp",EDGE,"E82.0")}),-1.0]])]});
            extrude(context, id + "F31", {"entities" : qUnion([Q0, Q1, Q2]), "depth" : 6 * mm});
        }
        {
            var Q0;
            {var subQ0=sQuery(id+"F6.wireOp",EDGE,"E12");Q0=makeQuery(id+"F8.boolean.opBoolean","MERGE",FACE,{"derivedFrom":[makeQuery(id+"F7.opExtrude","CAP_FACE",FACE,{"disambiguationData":[OSD([subQ0,sQuery(id+"F6.wireOp",EDGE,"E13"),sQuery(id+"F6.wireOp",EDGE,"E17"),sQuery(id+"F6.wireOp",EDGE,"E18"),sQuery(id+"F6.wireOp",EDGE,"E20.1.0"),sQuery(id+"F6.wireOp",EDGE,"E20.2.0"),sQuery(id+"F6.wireOp",EDGE,"E20.3.0")])],"isStart":true}),makeQuery(id+"F8.opExtrude","CAP_FACE",FACE,{"disambiguationData":[OSD([sQuery(id+"F0.wireOp",EDGE,"E0"),subQ0,sQuery(id+"F6.wireOp",EDGE,"E19.rect.bottom"),sQuery(id+"F6.wireOp",EDGE,"E19.rect.top"),sQuery(id+"F6.wireOp",EDGE,"E19.rect.left")])],"isStart":true})]});}
            var sketch = newSketch(context, id + "F32", { "sketchPlane" : qUnion([Q0])});
            skCircle(sketch, "E84.0", {"center": v(0, 0) * mm, "radius": 5.5 * mm});
            skCircle(sketch, "E85", {"center": v(0, 0) * mm, "radius": 8.5 * mm});
            skSolve(sketch);
        }
        {
            var Q0;
            Q0=makeQuery(id+"F25.opRevolve","SWEPT_FACE",FACE,{"disambiguationData":[OSD([sQuery(id+"F24.wireOp",EDGE,"E69")])]});
            var sketch = newSketch(context, id + "F33", { "sketchPlane" : qUnion([Q0])});
            skCircle(sketch, "E86.0", {"center": v(0, 30) * mm, "radius": 1.25 * mm});
            skLineSegment(sketch, "E87", {"start": v(0, 27.25) * mm, "end": v(13, 27.25) * mm});
            skLineSegment(sketch, "E88", {"start": v(13, 27.25) * mm, "end": v(10.5, 30.75) * mm});
            skLineSegment(sketch, "E89", {"start": v(10.5, 30.75) * mm, "end": v(-0.63, 32.93) * mm});
            skLineSegment(sketch, "E90", {"start": v(-0.63, 32.93) * mm, "end": v(-12.2, 24.7) * mm});
            skLineSegment(sketch, "E91", {"start": v(-12.2, 24.7) * mm, "end": v(-11, 22.25) * mm});
            skLineSegment(sketch, "E92", {"start": v(-11, 22.25) * mm, "end": v(0, 27.25) * mm});
            skCircle(sketch, "E93", {"center": v(0, 30) * mm, "radius": 2.25 * mm});
            skCircle(sketch, "E94", {"center": v(0, 30) * mm, "radius": 2.75 * mm});
            skSolve(sketch);
        }
        {
            var Q0;
            Q0=makeQuery(id+"F32.imprint","IMPRINT",FACE,{"disambiguationData":[TD([[makeQuery(id+"F32.imprint","IMPRINT",EDGE,{"derivedFrom":sQuery(id+"F32.wireOp",EDGE,"E85")}),1.0]])]});
            var Q1;
            {var subQ1=makeQuery(id+"F8.opExtrude","CAP_EDGE",EDGE,{"disambiguationData":[OSD([sQuery(id+"F6.wireOp",EDGE,"E19.rect.bottom")])],"isStart":true});Q1=makeQuery(id+"F32.imprint","IMPRINT",FACE,{"disambiguationData":[TD([[makeQuery(id+"F32.imprint","IMPRINT",EDGE,{"derivedFrom":subQ1}),-1.0]])]});}
            extrude(context, id + "F34", {"entities" : qUnion([Q0, Q1]), "depth" : 5 * mm});
        }
        {
            var Q0;
            Q0=qCreatedBy(makeId("Front.planeOp"),FACE);
            var sketch = newSketch(context, id + "F35", { "sketchPlane" : qUnion([Q0])});
            skLineSegment(sketch, "E95.0", {"start": v(-97, 8.5) * mm, "end": v(-97, -8.5) * mm});
            skLineSegment(sketch, "E95.1", {"start": v(-102, 8.5) * mm, "end": v(-102, -8.5) * mm});
            skLineSegment(sketch, "E96", {"start": v(-97, 0) * mm, "end": v(-102, 0) * mm, "construction": true});
            skCircle(sketch, "E97", {"center": v(-99.5, 0) * mm, "radius": 1.5 * mm});
            skSolve(sketch);
        }
        {
            var Q0;
            Q0=makeQuery(id+"F35.imprint","IMPRINT",FACE,{"disambiguationData":[TD([[makeQuery(id+"F35.imprint","IMPRINT",EDGE,{"derivedFrom":sQuery(id+"F35.wireOp",EDGE,"E97")}),1.0]])]});
            extrude(context, id + "F36", {"entities" : qUnion([Q0]), "operationType" : NewBodyOperationType.REMOVE, "oppositeDirection" : true, "depth" : 8.5 * mm});
        }
        {
            var Q0;
            {var subQ4=sQuery(id+"F33.wireOp",EDGE,"E91");Q0=makeQuery(id+"F33.imprint","IMPRINT",FACE,{"disambiguationData":[TD([[makeQuery(id+"F33.imprint","IMPRINT",EDGE,{"derivedFrom":subQ4}),1.0]])]});}
            var Q1;
            Q1=makeQuery(id+"F33.imprint","IMPRINT",FACE,{"disambiguationData":[TD([[makeQuery(id+"F33.imprint","IMPRINT",EDGE,{"derivedFrom":sQuery(id+"F33.wireOp",EDGE,"E93")}),-1.0]])]});
            var Q2;
            {var subQ3=sQuery(id+"F33.wireOp",EDGE,"E87");Q2=makeQuery(id+"F33.imprint","IMPRINT",FACE,{"disambiguationData":[TD([[makeQuery(id+"F33.imprint","IMPRINT",EDGE,{"derivedFrom":subQ3}),1.0]])]});}
            extrude(context, id + "F37", {"entities" : qUnion([Q0, Q1, Q2]), "depth" : 3 * mm});
        }
        {
            var Q0;
            Q0=makeQuery(id+"F33.imprint","IMPRINT",FACE,{"disambiguationData":[TD([[makeQuery(id+"F33.imprint","IMPRINT",EDGE,{"derivedFrom":sQuery(id+"F33.wireOp",EDGE,"E86.0")}),-1.0]])]});
            extrude(context, id + "F38", {"entities" : qUnion([Q0]), "operationType" : NewBodyOperationType.ADD, "depth" : 1.5 * mm});
        }
    });
